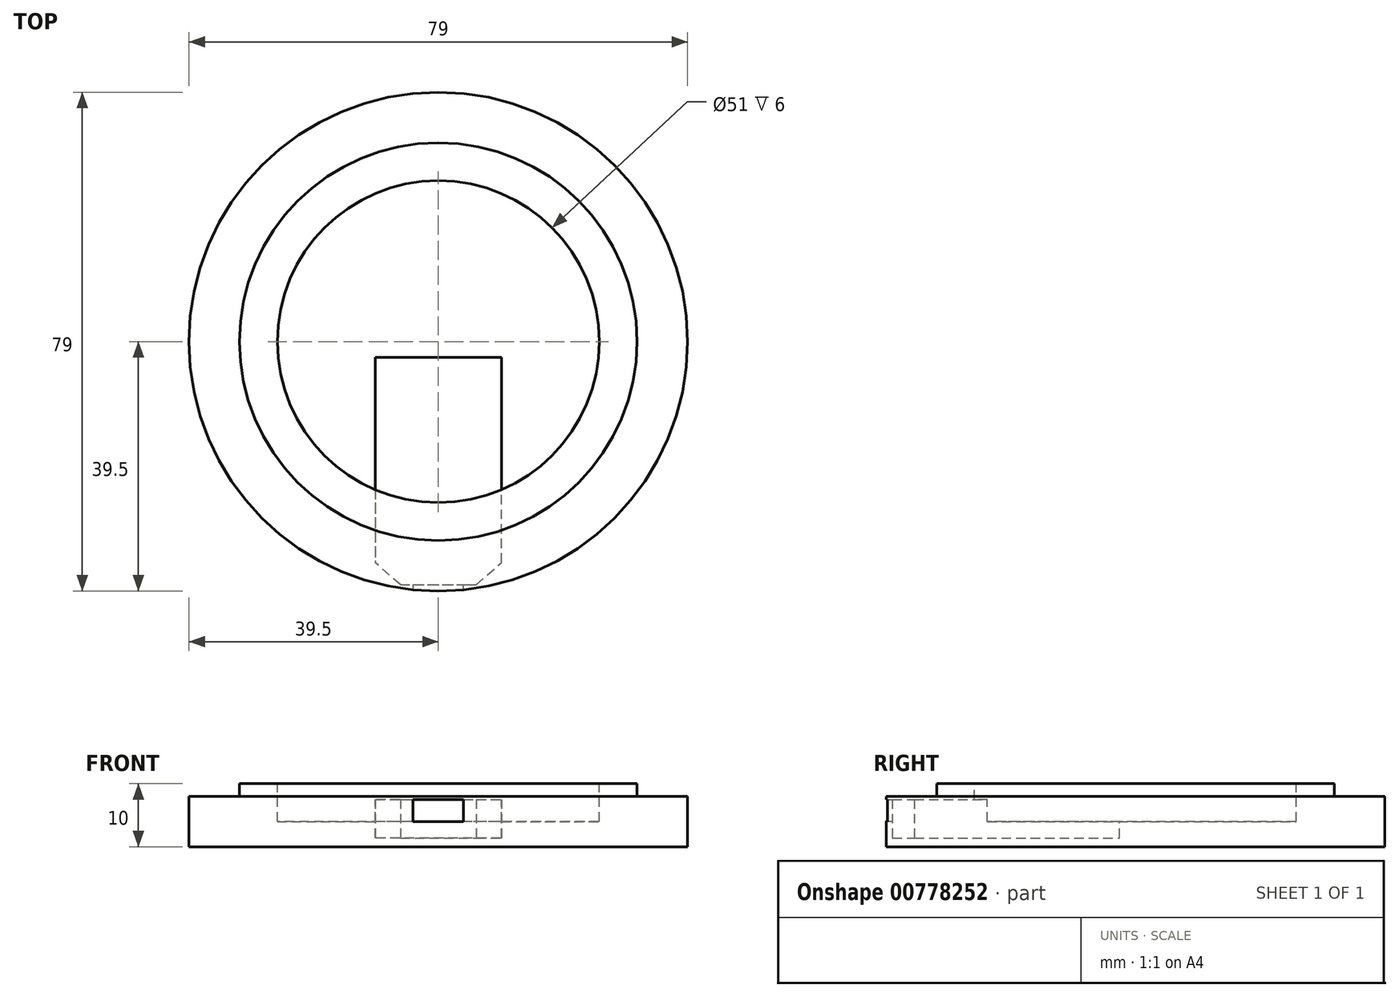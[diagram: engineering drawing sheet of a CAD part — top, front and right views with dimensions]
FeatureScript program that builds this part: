
annotation { "Feature Type Name" : "Feature", "Feature Type Description" : "" }
export const myFeature = defineFeature(function(context is Context, id is Id, definition is map)
    precondition{}
    {
        {
            var Q0;
            Q0=qCreatedBy(makeId("Front.planeOp"),FACE);
            var sketch = newSketch(context, id + "F0", { "sketchPlane" : qUnion([Q0])});
            skLineSegment(sketch, "E0", {"start": v(-39.5, 0) * mm, "end": v(-39.5, 8) * mm});
            skLineSegment(sketch, "E1", {"start": v(-39.5, 0) * mm, "end": v(0, 0) * mm});
            skLineSegment(sketch, "E2", {"start": v(-39.5, 8) * mm, "end": v(-31.5, 8) * mm});
            skLineSegment(sketch, "E3", {"start": v(-31.5, 10) * mm, "end": v(-31.5, 8) * mm});
            skLineSegment(sketch, "E4", {"start": v(-31.5, 10) * mm, "end": v(-25.5, 10) * mm});
            skLineSegment(sketch, "E5", {"start": v(-25.5, 10) * mm, "end": v(-25.5, 4) * mm});
            skLineSegment(sketch, "E6", {"start": v(-25.5, 4) * mm, "end": v(0, 4) * mm});
            skLineSegment(sketch, "E7", {"start": v(0, 4) * mm, "end": v(0, 0) * mm});
            skLineSegment(sketch, "E8", {"start": v(0, 45.26) * mm, "end": v(0, -35.39) * mm, "construction": true});
            skSolve(sketch);
        }
        {
            var Q0;
            Q0 = qSketchRegion(id + "F0", true);
            var Q1;
            Q1=sQuery(id+"F0.wireOp",EDGE,"E8");
            revolve(context, id + "F1", {"surfaceOperationType" : NewSurfaceOperationType.NEW, "entities" : qUnion([Q0]), "axis" : qUnion([Q1]), "revolveType" : RevolveType.FULL});
        }
        {
            var Q0;
            Q0=makeQuery(id+"F1.opRevolve","SWEPT_FACE",FACE,{"disambiguationData":[OSD([sQuery(id+"F0.wireOp",EDGE,"E6")])]});
            var sketch = newSketch(context, id + "F2", { "sketchPlane" : qUnion([Q0])});
            skLineSegment(sketch, "E9", {"start": v(10, -2.5) * mm, "end": v(-10, -2.5) * mm});
            skLineSegment(sketch, "E10", {"start": v(-10, -2.5) * mm, "end": v(-10, -38.5) * mm});
            skLineSegment(sketch, "E11", {"start": v(-10, -38.5) * mm, "end": v(10, -38.5) * mm});
            skLineSegment(sketch, "E12", {"start": v(10, -38.5) * mm, "end": v(10, -2.5) * mm});
            skLineSegment(sketch, "E13", {"start": v(0, 0) * mm, "end": v(0, -42.77) * mm, "construction": true});
            skLineSegment(sketch, "E14", {"start": v(-4, -38.5) * mm, "end": v(-4, -38.85) * mm});
            skLineSegment(sketch, "E15", {"start": v(-4, -38.85) * mm, "end": v(4, -38.85) * mm});
            skLineSegment(sketch, "E16", {"start": v(4, -38.8) * mm, "end": v(4, -38.5) * mm});
            skLineSegment(sketch, "E17", {"start": v(-4, -38.85) * mm, "end": v(-4, -39.5) * mm});
            skLineSegment(sketch, "E18", {"start": v(-4, -39.5) * mm, "end": v(4, -39.5) * mm});
            skLineSegment(sketch, "E19", {"start": v(4, -39.5) * mm, "end": v(4, -38.8) * mm});
            skLineSegment(sketch, "E20", {"start": v(-6, -38.5) * mm, "end": v(-10, -35) * mm});
            skLineSegment(sketch, "E21", {"start": v(6, -38.5) * mm, "end": v(10, -35) * mm});
            skSolve(sketch);
        }
        {
            var Q0;
            {var subQ0=sQuery(id+"F2.wireOp",EDGE,"E15");Q0=makeQuery(id+"F2.imprint","IMPRINT",FACE,{"disambiguationData":[TD([[makeQuery(id+"F2.imprint","IMPRINT",EDGE,{"derivedFrom":subQ0}),-1.0]])]});}
            var Q1;
            {var subQ2=sQuery(id+"F2.wireOp",EDGE,"E14");Q1=makeQuery(id+"F2.imprint","IMPRINT",FACE,{"disambiguationData":[TD([[makeQuery(id+"F2.imprint","IMPRINT",EDGE,{"derivedFrom":subQ2}),1.0]])]});}
            var Q2;
            {var subQ0=sQuery(id+"F2.wireOp",EDGE,"E9");Q2=makeQuery(id+"F2.imprint","IMPRINT",FACE,{"disambiguationData":[TD([[makeQuery(id+"F2.imprint","IMPRINT",EDGE,{"derivedFrom":subQ0}),1.0]])]});}
            var Q3;
            {var subQ3=sQuery(id+"F2.wireOp",EDGE,"E20");Q3=makeQuery(id+"F2.imprint","IMPRINT",FACE,{"disambiguationData":[TD([[makeQuery(id+"F2.imprint","IMPRINT",EDGE,{"derivedFrom":subQ3}),-1.0]])]});}
            extrude(context, id + "F3", {"entities" : qUnion([Q0, Q1, Q2, Q3]), "operationType" : NewBodyOperationType.REMOVE, "depth" : 3.5 * mm, "offsetDistance" : 25 * mm});
        }
        {
            var Q0;
            {var subQ0=sQuery(id+"F2.wireOp",EDGE,"E9");Q0=makeQuery(id+"F2.imprint","IMPRINT",FACE,{"disambiguationData":[TD([[makeQuery(id+"F2.imprint","IMPRINT",EDGE,{"derivedFrom":subQ0}),1.0]])]});}
            var Q1;
            {var subQ3=sQuery(id+"F2.wireOp",EDGE,"E20");Q1=makeQuery(id+"F2.imprint","IMPRINT",FACE,{"disambiguationData":[TD([[makeQuery(id+"F2.imprint","IMPRINT",EDGE,{"derivedFrom":subQ3}),-1.0]])]});}
            extrude(context, id + "F4", {"entities" : qUnion([Q0, Q1]), "operationType" : NewBodyOperationType.REMOVE, "oppositeDirection" : true, "depth" : 2.6 * mm, "offsetDistance" : 25 * mm});
        }
    });
